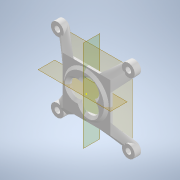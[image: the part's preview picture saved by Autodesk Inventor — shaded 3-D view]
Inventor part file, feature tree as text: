
AUTODESK INVENTOR PART (.ipt)
format: ipt  version: 2021 (Build 250183000, 183)  size: 327,680 bytes
history: native  units: mm
features: sketch x9, reference x8, extrude x5, other x4, plane x3, chamfer x2, mirror x2, loft x1, hole x1
ambient origin geometry x8: Origin, YZ Plane, XZ Plane, XY Plane, X Axis, Y Axis, Z Axis, Center Point
bodies: Solid1 (feature_tree)
feature tree (35):
  extrude  "Extrusion1"  Depth=25.0mm
  extrude  "Extrusion2"  Depth=10.5mm
  extrude  "Extrusion3"  Depth=10.5mm
  extrude  "Extrusion4"  Depth=10.0mm
  chamfer  "Chamfer2"  Distance=1.5mm
  chamfer  "Chamfer3"  Distance=1.5mm
  plane  "Work Plane1"
  sketch  "Sketch6"  dims[d15=30.0mm]
  sketch  "Sketch7"  dims[d16=30.0mm]
  loft  "Loft1"
  extrude  "Extrusion5"  Depth=7.0mm
  hole  "Hole1"  [1 undecoded]
  plane  "Work Plane2"
  mirror  "Mirror1"
  plane  "Work Plane3"
  mirror  "Mirror2"
  sketch  "Sketch1"  dims[d0=20.0mm d1=25.0mm]
  sketch  "Sketch2"  dims[d2=3.0mm d3=0.0mm d4=10.5mm]
  sketch  "Sketch3"  dims[d5=10.5mm d6=10.5mm]
  sketch  "Sketch5"  dims[d7=10.0mm d8=0.0mm d12=20.7mm d13=1.5mm d14=0.0mm]
  reference  "Reference1"
  reference  "Reference2"
  reference  "Reference3"
  reference  "Reference4"
  reference  "Reference5"
  reference  "Reference6"
  reference  "Reference7"
  reference  "Reference8"
  sketch  "Sketch8"  dims[d17=15.0mm]
  sketch  "Sketch9"  dims[d18=15.0mm d19=1.5mm d20=0.0mm]
  sketch  "Sketch10"  dims[d21=1.5mm d22=2.0mm d23=45.0deg d24=1.5mm d25=2.0mm d26=45.0deg d27=7.0mm d28=7.0mm d29=0.0mm d30=90.0deg d31=0.0mm d32=90.0deg d33=4.0mm d34=0.0mm d35=3.5mm d36=6.0mm d37=4.0mm d38=2.0mm d39=90.0deg d40=8.0mm d41=20.594885mm d9=0.5mm d10=0.872665mm]
  parser-record x1  (decoder bookkeeping rows leaked as tree rows — omitted from the tree; the rows remain in map.json)
  other  "Heatsink Holder.iam"
  other  "Back:1"
  other  "Heatsink:1"
note: 1 required parameter value undecoded (feature->parameter linkage not recoverable at this tier; creation-order binding heuristic only, values carry confidence <= 0.55)
note: 1 file-system path scrubbed to <path> (originals preserved in map.json)
